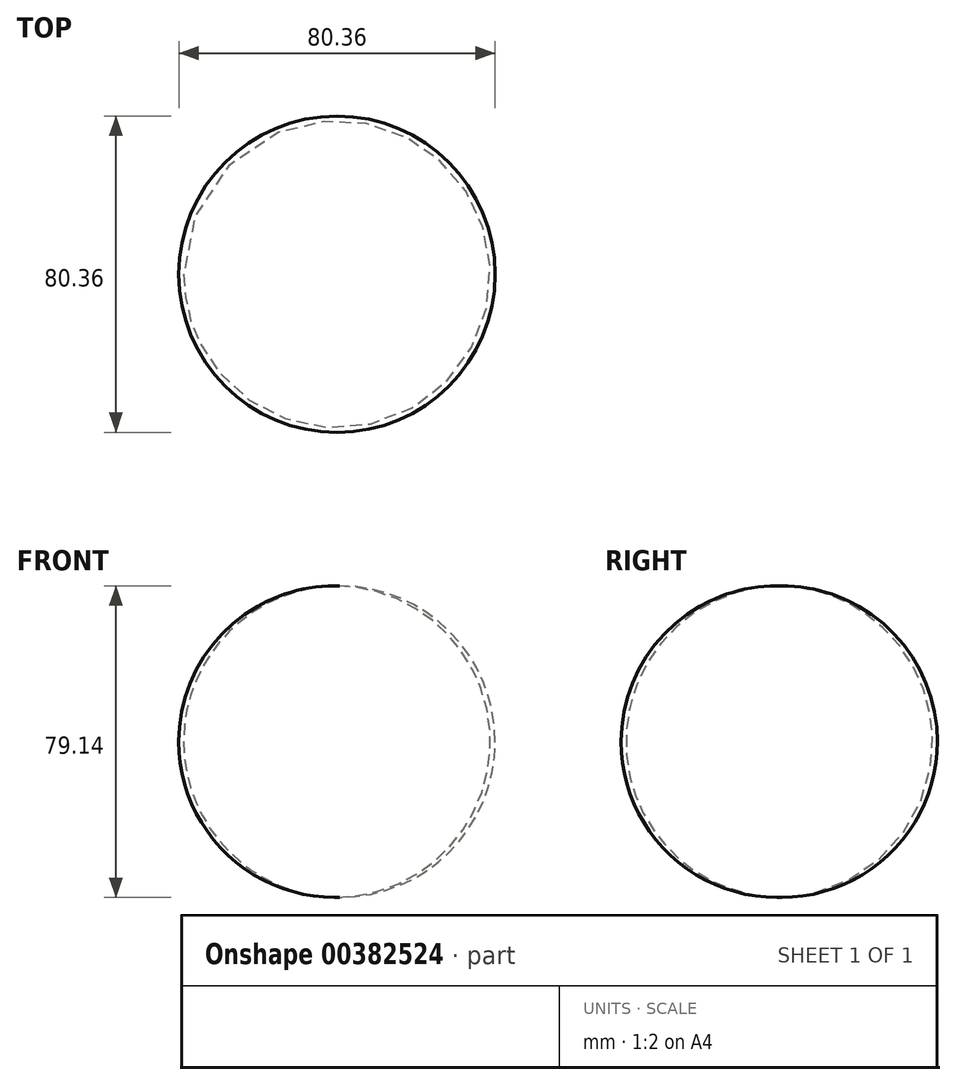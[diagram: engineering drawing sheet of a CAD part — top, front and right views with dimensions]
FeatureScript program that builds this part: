
annotation { "Feature Type Name" : "Feature", "Feature Type Description" : "" }
export const myFeature = defineFeature(function(context is Context, id is Id, definition is map)
    precondition{}
    {
        {
            var Q0;
            Q0=qCreatedBy(makeId("Front.planeOp"),FACE);
            var sketch = newSketch(context, id + "F0", { "sketchPlane" : qUnion([Q0])});
            skLineSegment(sketch, "E0", {"start": v(0, 37.86) * mm, "end": v(0, -41.26) * mm});
            skArc(sketch, "E1", {"start": v(0, 37.86) * mm, "mid": v(-40.18, -1.7) * mm, "end": v(0, -41.26) * mm});
            skLineSegment(sketch, "E2", {"start": v(0, 37.86) * mm, "end": v(0, -41.26) * mm, "construction": true});
            skSolve(sketch);
        }
        {
            var Q0;
            Q0 = qSketchRegion(id + "F0", true);
            var Q1;
            Q1=sQuery(id+"F0.wireOp",EDGE,"E0");
            revolve(context, id + "F1", {"surfaceOperationType" : NewSurfaceOperationType.NEW, "entities" : qUnion([Q0]), "axis" : qUnion([Q1]), "revolveType" : RevolveType.FULL});
        }
    });
